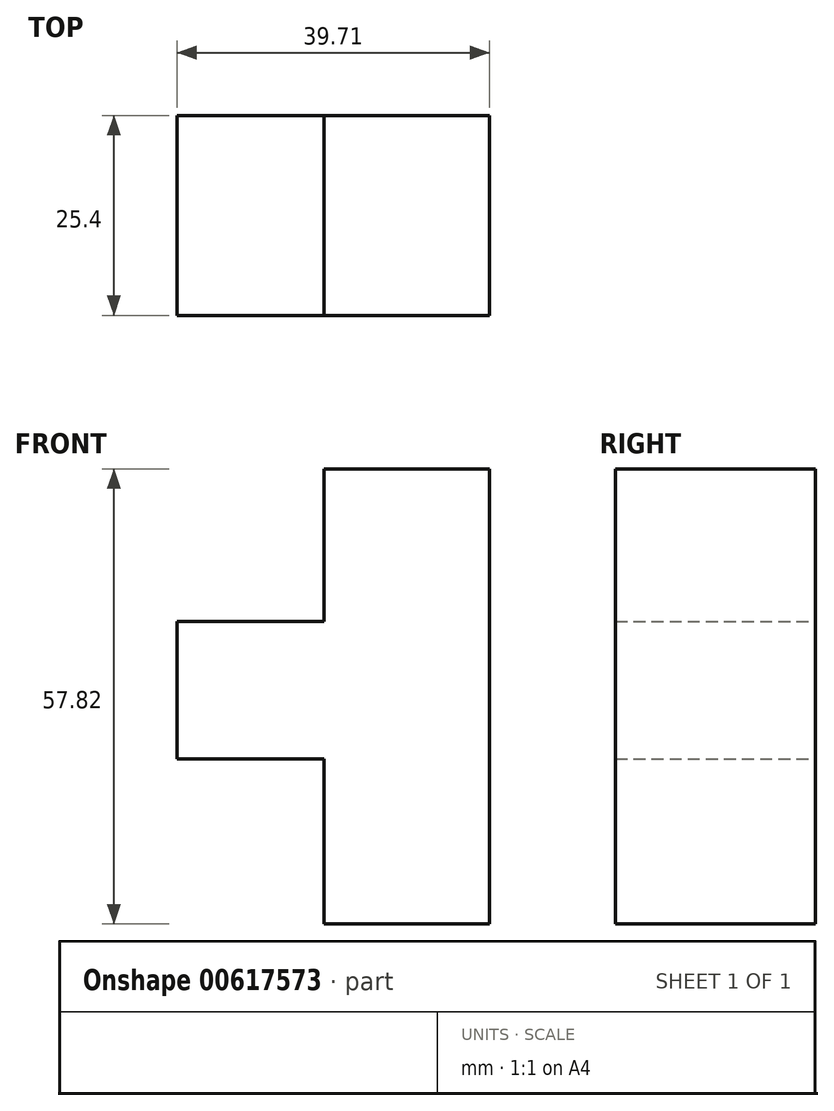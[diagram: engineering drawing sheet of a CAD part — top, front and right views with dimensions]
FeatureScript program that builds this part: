
annotation { "Feature Type Name" : "Feature", "Feature Type Description" : "" }
export const myFeature = defineFeature(function(context is Context, id is Id, definition is map)
    precondition{}
    {
        {
            var Q0;
            Q0=qCreatedBy(makeId("Front.planeOp"),FACE);
            var sketch = newSketch(context, id + "F0", { "sketchPlane" : qUnion([Q0])});
            skLineSegment(sketch, "E0", {"start": v(0, 0) * mm, "end": v(0, 57.82) * mm});
            skLineSegment(sketch, "E1", {"start": v(0, 57.82) * mm, "end": v(-21, 57.82) * mm});
            skLineSegment(sketch, "E2", {"start": v(-21, 57.82) * mm, "end": v(-21, 38.45) * mm});
            skLineSegment(sketch, "E3", {"start": v(-21, 38.45) * mm, "end": v(-39.7, 38.45) * mm});
            skLineSegment(sketch, "E4", {"start": v(-39.7, 38.45) * mm, "end": v(-39.7, 20.95) * mm});
            skLineSegment(sketch, "E5", {"start": v(-39.7, 20.95) * mm, "end": v(-21, 20.95) * mm});
            skLineSegment(sketch, "E6", {"start": v(-21, 20.95) * mm, "end": v(-21, 0) * mm});
            skLineSegment(sketch, "E7", {"start": v(-21, 0) * mm, "end": v(0, 0) * mm});
            skSolve(sketch);
        }
        {
            var Q0;
            Q0 = qSketchRegion(id + "F0", true);
            extrude(context, id + "F1", {"entities" : qUnion([Q0]), "depth" : 25.4 * mm, "offsetDistance" : 25.4 * mm});
        }
    });
